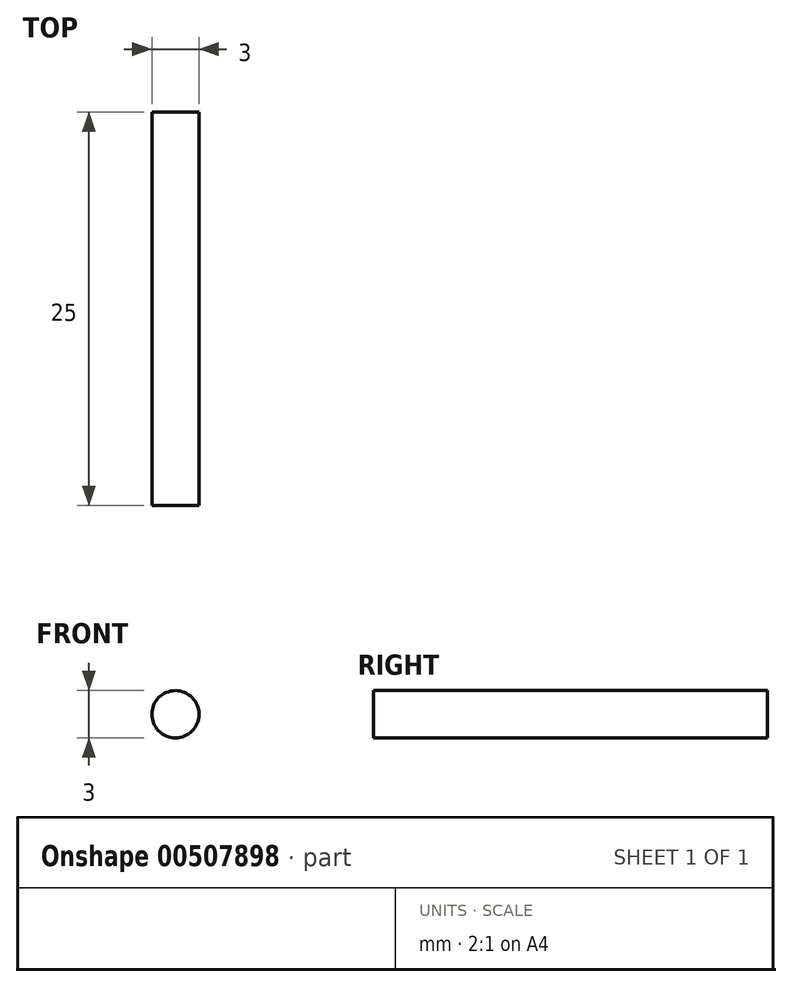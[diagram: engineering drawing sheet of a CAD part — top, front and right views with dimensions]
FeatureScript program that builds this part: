
annotation { "Feature Type Name" : "Feature", "Feature Type Description" : "" }
export const myFeature = defineFeature(function(context is Context, id is Id, definition is map)
    precondition{}
    {
        {
            var Q0;
            Q0=qCreatedBy(makeId("Front.planeOp"),FACE);
            var sketch = newSketch(context, id + "F0", { "sketchPlane" : qUnion([Q0])});
            skCircle(sketch, "E0", {"center": v(0, 0) * mm, "radius": 1.5 * mm});
            skSolve(sketch);
        }
        {
            var Q0;
            Q0=makeQuery(id+"F0.imprint","IMPRINT",FACE,{"disambiguationData":[TD([[makeQuery(id+"F0.imprint","IMPRINT",EDGE,{"derivedFrom":sQuery(id+"F0.wireOp",EDGE,"E0")}),1.0]])]});
            extrude(context, id + "F1", {"entities" : qUnion([Q0]), "depth" : 25 * mm, "offsetDistance" : 25 * mm, "symmetric" : true});
        }
    });
